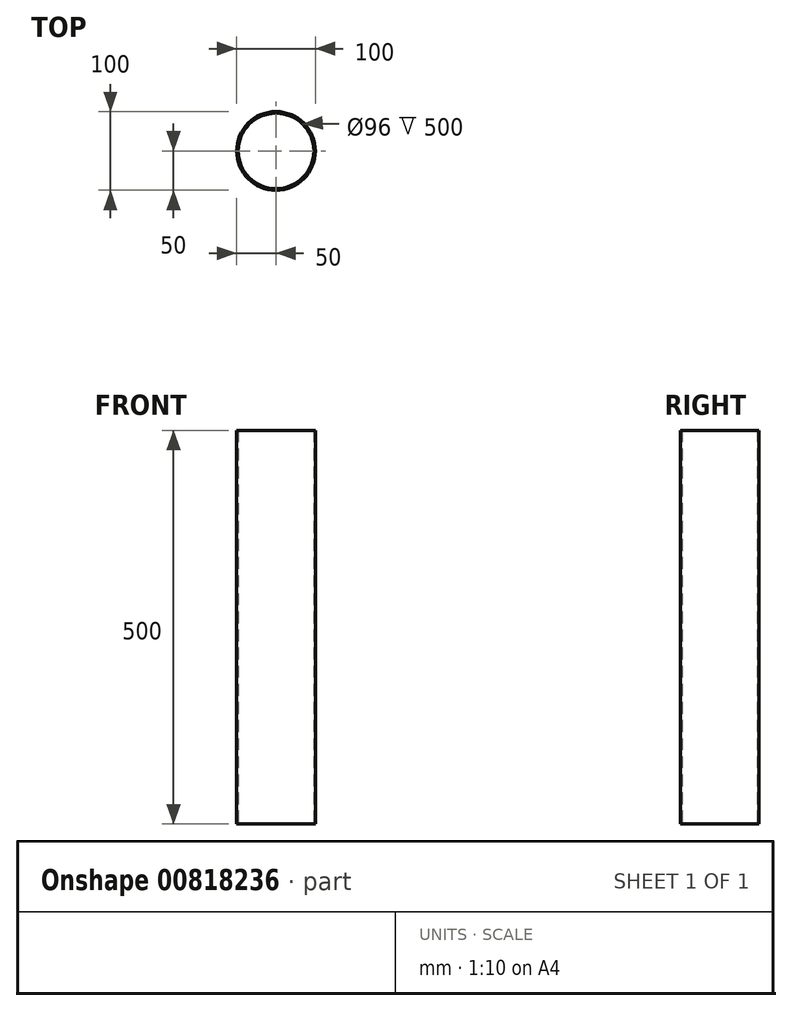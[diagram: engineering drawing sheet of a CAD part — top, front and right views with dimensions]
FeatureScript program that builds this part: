
annotation { "Feature Type Name" : "Feature", "Feature Type Description" : "" }
export const myFeature = defineFeature(function(context is Context, id is Id, definition is map)
    precondition{}
    {
        {
            var Q0;
            Q0=qCreatedBy(makeId("Top.planeOp"),FACE);
            var sketch = newSketch(context, id + "F0", { "sketchPlane" : qUnion([Q0])});
            skCircle(sketch, "E0", {"center": v(0, 0) * mm, "radius": 50 * mm});
            skCircle(sketch, "E1.0", {"center": v(0, 0) * mm, "radius": 48 * mm});
            skSolve(sketch);
        }
        {
            var Q0;
            Q0 = qSketchRegion(id + "F0", true);
            extrude(context, id + "F1", {"entities" : qUnion([Q0]), "depth" : 500 * mm, "offsetDistance" : 25 * mm});
        }
    });
